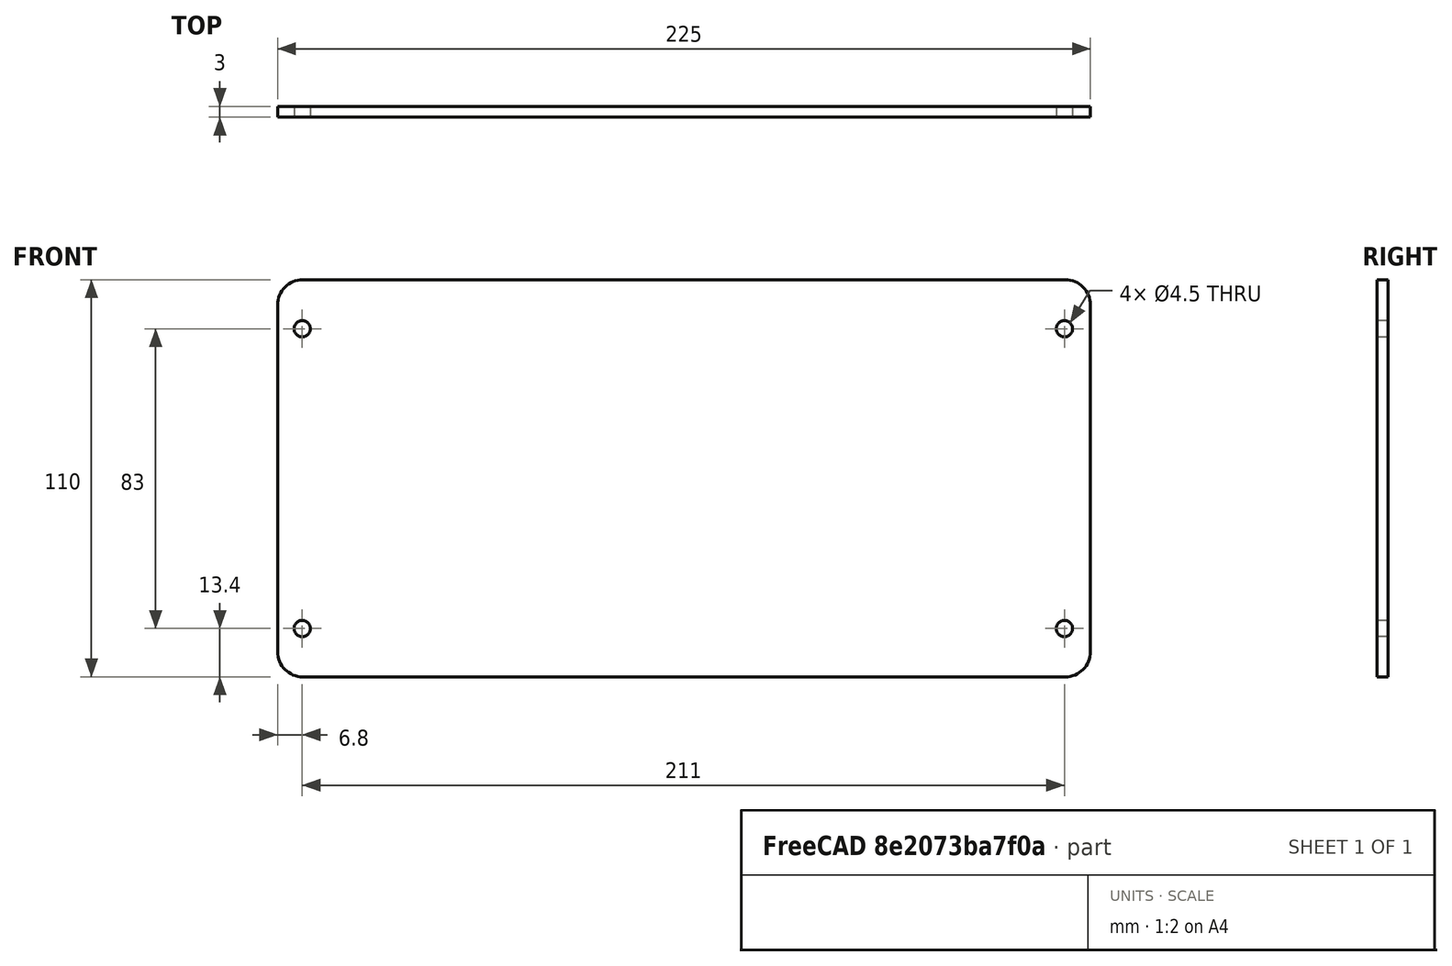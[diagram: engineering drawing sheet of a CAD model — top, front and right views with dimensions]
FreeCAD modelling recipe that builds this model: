
FCSTD DOCUMENT  (FreeCAD 0.18R4 (GitTag))
Label: CADBacking
License: All rights reserved
LicenseURL: http://en.wikipedia.org/wiki/All_rights_reserved
objects: Part::Cylinder×4, Part::Fuse×3, Part::Box×1, Part::Fillet×1, Part::Cut×1
note: 10 computed .brp shape members not serialized (recipe doc carries the construction recipe); baked Part::Feature solids carry a one-line shape summary decoded from their .brp

FEATURE [Part::Box] Box  label="Cube"
  AttacherType = Attacher::AttachEngine3D
  Height = 110
  Length = 225
  Width = 3
FEATURE [Part::Fillet] Fillet
  Base = -> Box
  Edges = 4 edges r=7: [Edge2,Edge4,Edge6,Edge8]
FEATURE [Part::Cylinder] Cylinder
  Angle = 360
  AttacherType = Attacher::AttachEngine3D
  Height = 3
  Placement = pos=(6.8,-18,13.4) rot=(1,0,0;1.5708rad)
  Radius = 2.25
FEATURE [Part::Cylinder] Cylinder005
  Angle = 360
  AttacherType = Attacher::AttachEngine3D
  Height = 3
  Placement = pos=(6.8,-18,96.4) rot=(1,0,0;1.5708rad)
  Radius = 2.25
FEATURE [Part::Cylinder] Cylinder006
  Angle = 360
  AttacherType = Attacher::AttachEngine3D
  Height = 3
  Placement = pos=(217.8,-18,96.4) rot=(1,0,0;1.5708rad)
  Radius = 2.25
FEATURE [Part::Cylinder] Cylinder007
  Angle = 360
  AttacherType = Attacher::AttachEngine3D
  Height = 3
  Placement = pos=(217.8,-18,13.4) rot=(1,0,0;1.5708rad)
  Radius = 2.25
FEATURE [Part::Fuse] Fusion004
  Base = -> Cylinder
  Tool = -> Cylinder005
FEATURE [Part::Fuse] Fusion005
  Base = -> Cylinder006
  Tool = -> Cylinder007
FEATURE [Part::Fuse] Fusion006  label="Screw Holes"
  Base = -> Fusion004
  Placement = pos=(0,21,0) rot=(0,0,1;0rad)
  Tool = -> Fusion005
FEATURE [Part::Cut] Cut009
  Base = -> Fillet
  Tool = -> Fusion006
